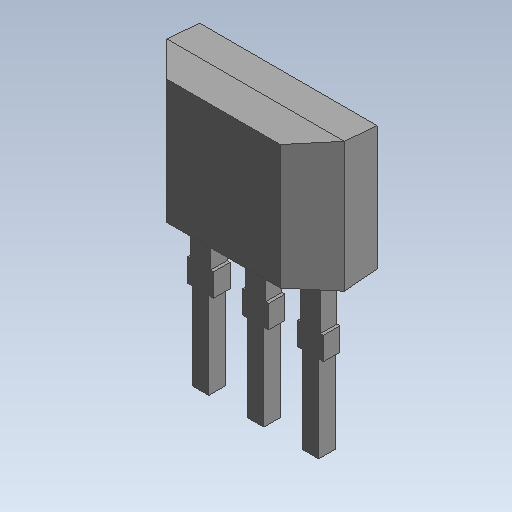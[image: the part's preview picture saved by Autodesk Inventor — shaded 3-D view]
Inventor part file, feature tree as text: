
AUTODESK INVENTOR PART (.ipt)
format: ipt  version: 2020 (Build 240168000, 168)  size: 78,848 bytes
history: native  units: mm (DEFAULTED — no unit token found)
features: extrude x1
ambient origin geometry x8: Origin, YZ Plane, XZ Plane, XY Plane, X Axis, Y Axis, Z Axis, Center Point
bodies: Solid1 (feature_tree)
feature tree (1):
  extrude  "Extrude2"  [1 undecoded]
note: 1 required parameter value undecoded (feature->parameter linkage not recoverable at this tier; creation-order binding heuristic only, values carry confidence <= 0.55)
